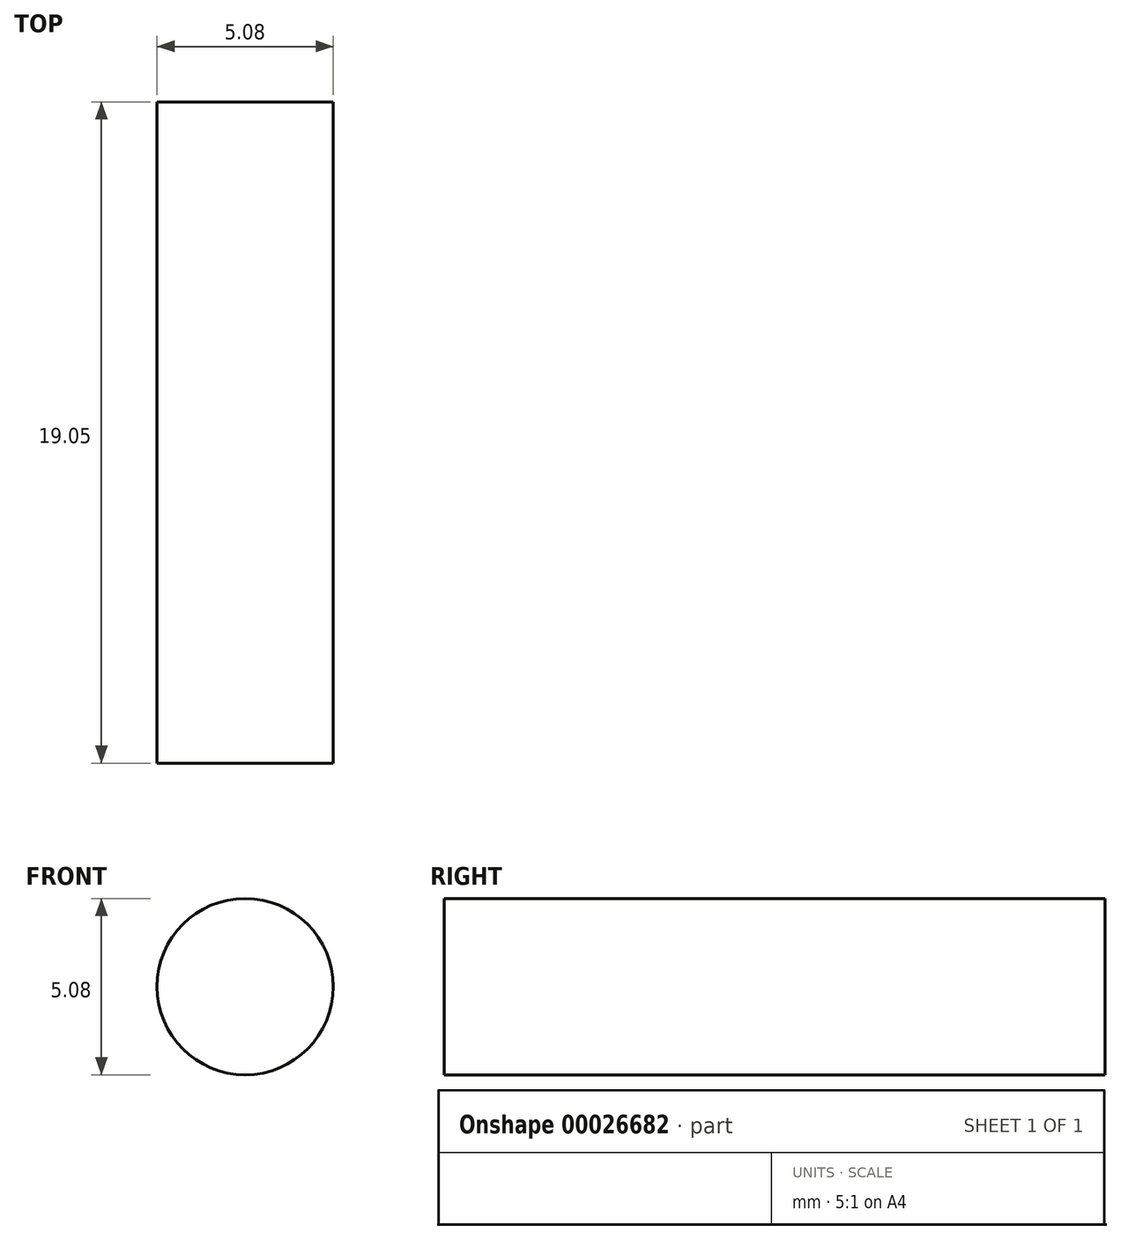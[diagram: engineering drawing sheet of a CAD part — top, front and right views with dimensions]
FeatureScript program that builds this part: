
annotation { "Feature Type Name" : "Feature", "Feature Type Description" : "" }
export const myFeature = defineFeature(function(context is Context, id is Id, definition is map)
    precondition{}
    {
        {
            var Q0;
            Q0=qCreatedBy(makeId("Front.planeOp"),FACE);
            var sketch = newSketch(context, id + "F0", { "sketchPlane" : qUnion([Q0])});
            skCircle(sketch, "E0", {"center": v(0, 0) * mm, "radius": 2.54 * mm});
            skSolve(sketch);
        }
        {
            var Q0;
            Q0=makeQuery(id+"F0.imprint","IMPRINT",FACE,{"disambiguationData":[TD([[makeQuery(id+"F0.imprint","IMPRINT",EDGE,{"derivedFrom":sQuery(id+"F0.wireOp",EDGE,"E0")}),1.0]])]});
            extrude(context, id + "F1", {"entities" : qUnion([Q0]), "depth" : 19.05 * mm});
        }
    });
